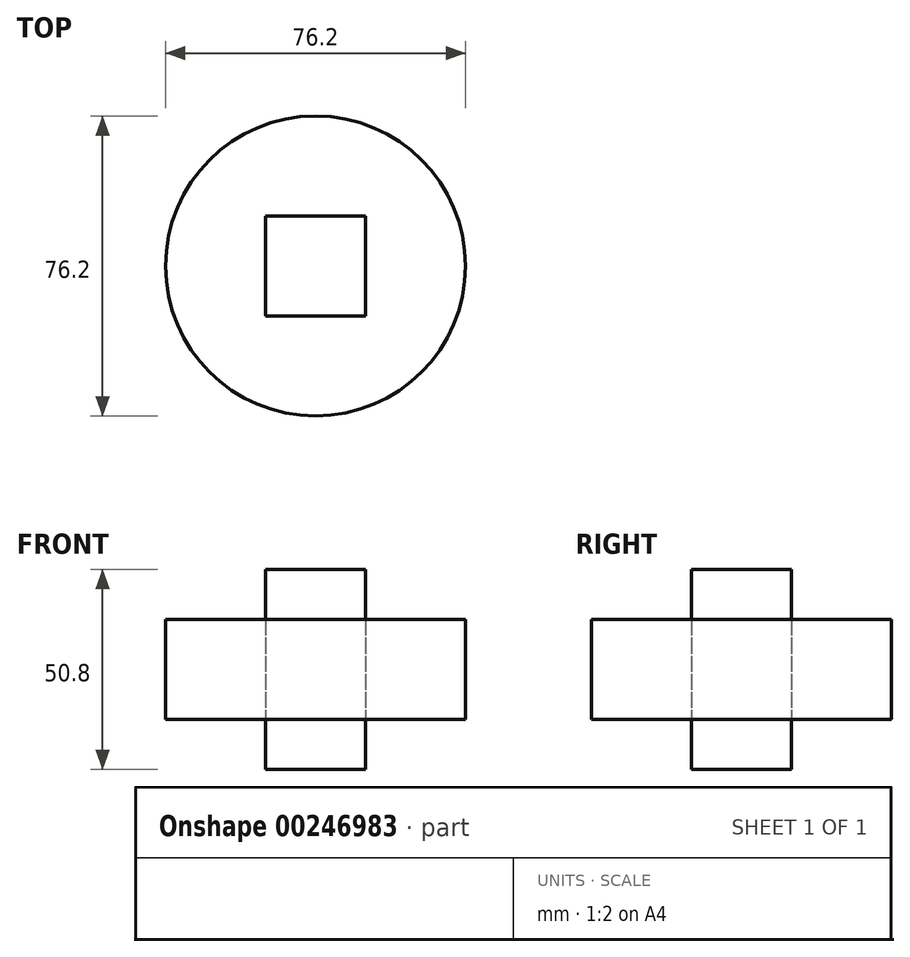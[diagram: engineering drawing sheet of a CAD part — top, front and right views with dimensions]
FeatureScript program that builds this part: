
annotation { "Feature Type Name" : "Feature", "Feature Type Description" : "" }
export const myFeature = defineFeature(function(context is Context, id is Id, definition is map)
    precondition{}
    {
        {
            var Q0;
            Q0=qCreatedBy(makeId("Top.planeOp"),FACE);
            var sketch = newSketch(context, id + "F0", { "sketchPlane" : qUnion([Q0])});
            skCircle(sketch, "E0", {"center": v(0, 0) * mm, "radius": 38.1 * mm});
            skSolve(sketch);
        }
        {
            var Q0;
            Q0 = qSketchRegion(id + "F0", true);
            extrude(context, id + "F1", {"entities" : qUnion([Q0]), "endBound" : BoundingType.SYMMETRIC, "depth" : 25.4 * mm});
        }
        {
            var Q0;
            Q0=qCreatedBy(makeId("Top.planeOp"),FACE);
            var sketch = newSketch(context, id + "F2", { "sketchPlane" : qUnion([Q0])});
            skLineSegment(sketch, "E1.bottom", {"start": v(12.7, 12.7) * mm, "end": v(-12.7, 12.7) * mm});
            skLineSegment(sketch, "E1.top", {"start": v(12.7, -12.7) * mm, "end": v(-12.7, -12.7) * mm});
            skLineSegment(sketch, "E1.left", {"start": v(12.7, 12.7) * mm, "end": v(12.7, -12.7) * mm});
            skLineSegment(sketch, "E1.right", {"start": v(-12.7, 12.7) * mm, "end": v(-12.7, -12.7) * mm});
            skPoint(sketch, "E1.middle", {"position": v(0, 0) * mm});
            skSolve(sketch);
        }
        {
            var Q0;
            Q0 = qSketchRegion(id + "F2", true);
            extrude(context, id + "F3", {"entities" : qUnion([Q0]), "endBound" : BoundingType.SYMMETRIC, "depth" : 50.8 * mm});
        }
        {
            var Q0;
            Q0=makeQuery(id+"F3.opExtrude","SWEPT_BODY",BODY,{"disambiguationData":[OSD([sQuery(id+"F2.wireOp",EDGE,"E1.bottom"),sQuery(id+"F2.wireOp",EDGE,"E1.top"),sQuery(id+"F2.wireOp",EDGE,"E1.left"),sQuery(id+"F2.wireOp",EDGE,"E1.right")])]});
            var Q1;
            Q1=makeQuery(id+"F1.opExtrude","SWEPT_BODY",BODY,{"disambiguationData":[OSD([sQuery(id+"F0.wireOp",EDGE,"E0")])]});
            var Q2;
            Q2=makeQuery(id+"F1.opExtrude","SWEPT_BODY",BODY,{"disambiguationData":[OSD([sQuery(id+"F0.wireOp",EDGE,"E0")])]});
            var Q3;
            Q3=makeQuery(id+"F3.opExtrude","SWEPT_FACE",FACE,{"disambiguationData":[OSD([sQuery(id+"F2.wireOp",EDGE,"E1.top")])]});
            var Q4;
            Q4=makeQuery(id+"F3.opExtrude","SWEPT_FACE",FACE,{"disambiguationData":[OSD([sQuery(id+"F2.wireOp",EDGE,"E1.bottom")])]});
            booleanBodies(context, id + "F4", {"operationType" : BooleanOperationType.INTERSECTION, "tools" : qUnion([Q0, Q1]), "targets" : qUnion([Q2]), "offset" : true, "entitiesToOffset" : qUnion([Q3, Q4]), "offsetDistance" : 6.35 * mm, "keepTools" : true});
        }
    });
